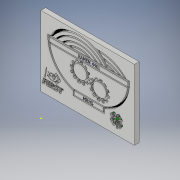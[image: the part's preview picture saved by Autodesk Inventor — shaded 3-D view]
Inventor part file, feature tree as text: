
AUTODESK INVENTOR PART (.ipt)
format: ipt  version: 2018 (Build 220112000, 112)  size: 1,004,544 bytes
history: native  units: in
note: dims shown in document units (in); Inventor stores cm internally (conversion verified against a paired STEP export)
features: sketch x10, emboss x6, other x4, extrude x2
ambient origin geometry x8: Origin, YZ Plane, XZ Plane, XY Plane, X Axis, Y Axis, Z Axis, Center Point
bodies: Solid1 (feature_tree)
feature tree (22):
  sketch  "Sketch1"  dims[d0=4.0in d1=4.0in]
  extrude  "Extrusion1"  Depth=4.0in
  emboss  "Emboss1"
  emboss  "Emboss2"
  emboss  "Emboss3"
  emboss  "Emboss4"
  emboss  "Emboss5"
  emboss  "Emboss6"
  sketch  "Sketch9"  dims[d79=1.0in]
  extrude  "Extrusion2"  Depth=0.1in TaperAngle=0.0deg
  sketch  "Sketch2"  dims[d2=0.2in d3=0.0in d15=0.1in d16=0.0in]
  sketch  "Sketch3"  dims[d17=0.0in d18=0.0in]
  other  "Image1"
  sketch  "Sketch4"  dims[d19=0.1in d20=0.0in]
  sketch  "Sketch5"  dims[d32=0.1in d33=0.0in]
  sketch  "Sketch6"  dims[d45=0.1in d46=0.0in]
  other  "Image2"
  sketch  "Sketch7"  dims[d66=135.0deg]
  other  "Image3"
  sketch  "Sketch8"  dims[d67=0.1in d68=0.0in]
  other  "Image4"
  sketch  "Sketch10"  dims[d80=0.5in d81=0.0in]
